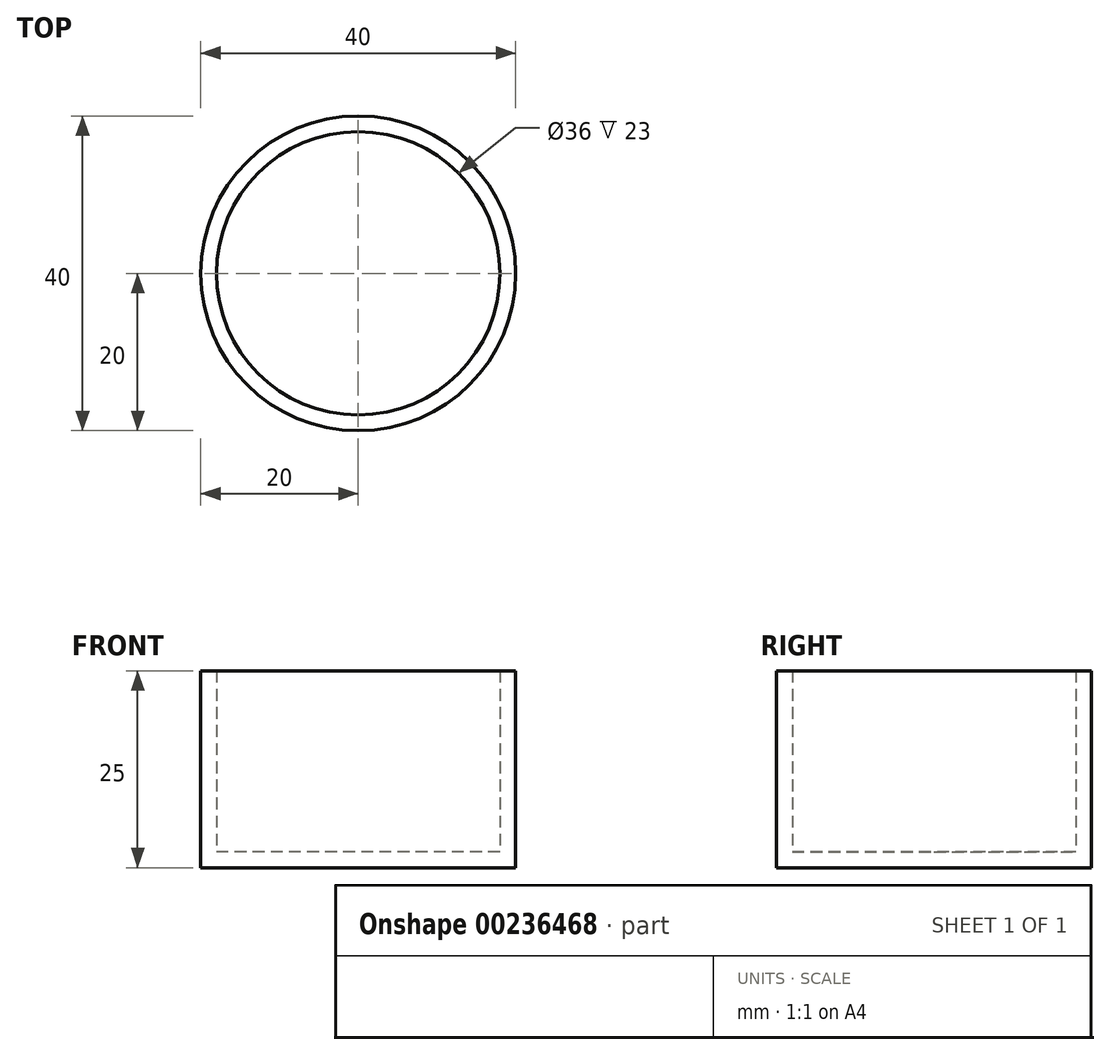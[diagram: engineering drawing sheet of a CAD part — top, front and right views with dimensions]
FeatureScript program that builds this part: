
annotation { "Feature Type Name" : "Feature", "Feature Type Description" : "" }
export const myFeature = defineFeature(function(context is Context, id is Id, definition is map)
    precondition{}
    {
        {
            var Q0;
            Q0=qCreatedBy(makeId("Top.planeOp"),FACE);
            var sketch = newSketch(context, id + "F0", { "sketchPlane" : qUnion([Q0])});
            skCircle(sketch, "E0", {"center": v(0, 0) * mm, "radius": 20 * mm});
            skCircle(sketch, "E1", {"center": v(0, 0) * mm, "radius": 18 * mm});
            skPoint(sketch, "E2", {"position": v(0, 18) * mm});
            skPoint(sketch, "E3", {"position": v(0, 20) * mm});
            skSolve(sketch);
        }
        {
            var Q0;
            Q0=makeQuery(id+"F0.imprint","IMPRINT",FACE,{"disambiguationData":[TD([[makeQuery(id+"F0.imprint","IMPRINT",EDGE,{"derivedFrom":sQuery(id+"F0.wireOp",EDGE,"E1")}),1.0]])]});
            extrude(context, id + "F1", {"entities" : qUnion([Q0]), "depth" : 2 * mm, "offsetDistance" : 25 * mm});
        }
        {
            var Q0;
            Q0=makeQuery(id+"F0.imprint","IMPRINT",FACE,{"disambiguationData":[TD([[makeQuery(id+"F0.imprint","IMPRINT",EDGE,{"derivedFrom":sQuery(id+"F0.wireOp",EDGE,"E0")}),1.0]])]});
            extrude(context, id + "F2", {"entities" : qUnion([Q0]), "operationType" : NewBodyOperationType.ADD, "depth" : 25 * mm, "offsetDistance" : 25 * mm});
        }
    });
